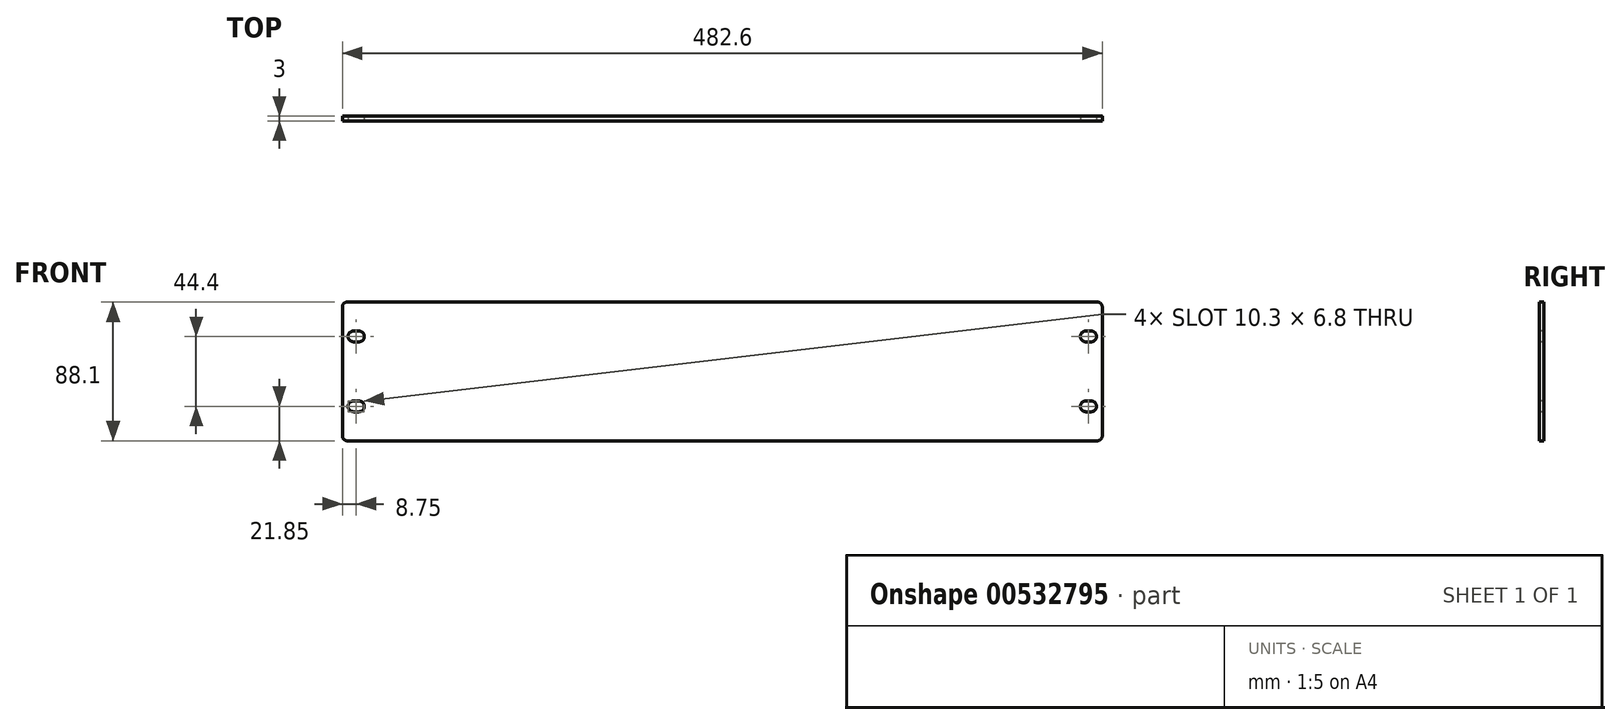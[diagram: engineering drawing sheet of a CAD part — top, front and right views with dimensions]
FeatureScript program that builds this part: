
annotation { "Feature Type Name" : "Feature", "Feature Type Description" : "" }
export const myFeature = defineFeature(function(context is Context, id is Id, definition is map)
    precondition{}
    {
        {
            var Q0;
            Q0=qCreatedBy(makeId("Front.planeOp"),FACE);
            var sketch = newSketch(context, id + "F0", { "sketchPlane" : qUnion([Q0])});
            skLineSegment(sketch, "E0.bottom", {"start": v(241.3, -44.05) * mm, "end": v(-241.3, -44.05) * mm});
            skLineSegment(sketch, "E0.top", {"start": v(241.3, 44.05) * mm, "end": v(-241.3, 44.05) * mm});
            skLineSegment(sketch, "E0.left", {"start": v(241.3, -44.05) * mm, "end": v(241.3, 44.05) * mm});
            skLineSegment(sketch, "E0.right", {"start": v(-241.3, -44.05) * mm, "end": v(-241.3, 44.05) * mm});
            skPoint(sketch, "E0.middle", {"position": v(0, 0) * mm});
            skSolve(sketch);
        }
        {
            var Q0;
            Q0=makeQuery(id+"F0.imprint","IMPRINT",FACE,{"disambiguationData":[TD([[makeQuery(id+"F0.imprint","IMPRINT",EDGE,{"derivedFrom":sQuery(id+"F0.wireOp",EDGE,"E0.bottom")}),-1.0]])]});
            extrude(context, id + "F1", {"entities" : qUnion([Q0]), "oppositeDirection" : true, "depth" : 3 * mm, "offsetDistance" : 25 * mm});
        }
        {
            var Q0;
            Q0=makeQuery(id+"F1.opExtrude","SWEPT_EDGE",EDGE,{"disambiguationData":[OSD([sQuery(id+"F0.wireOp",EDGE,"E0.top"),sQuery(id+"F0.wireOp",EDGE,"E0.right")])]});
            var Q1;
            Q1=makeQuery(id+"F1.opExtrude","SWEPT_EDGE",EDGE,{"disambiguationData":[OSD([sQuery(id+"F0.wireOp",EDGE,"E0.top"),sQuery(id+"F0.wireOp",EDGE,"E0.left")])]});
            var Q2;
            Q2=makeQuery(id+"F1.opExtrude","SWEPT_EDGE",EDGE,{"disambiguationData":[OSD([sQuery(id+"F0.wireOp",EDGE,"E0.bottom"),sQuery(id+"F0.wireOp",EDGE,"E0.left")])]});
            var Q3;
            Q3=makeQuery(id+"F1.opExtrude","SWEPT_EDGE",EDGE,{"disambiguationData":[OSD([sQuery(id+"F0.wireOp",EDGE,"E0.bottom"),sQuery(id+"F0.wireOp",EDGE,"E0.right")])]});
            fillet(context, id + "F2", {"entities" : qUnion([Q0, Q1, Q2, Q3]), "radius" : 3 * mm, "tangentPropagation" : true, "allowEdgeOverflow" : false});
        }
        {
            var Q0;
            Q0=qCreatedBy(makeId("Front.planeOp"),FACE);
            var sketch = newSketch(context, id + "F3", { "sketchPlane" : qUnion([Q0])});
            skArc(sketch, "E1", {"start": v(-230.8, 18.8) * mm, "mid": v(-227.4, 22.2) * mm, "end": v(-230.8, 25.6) * mm});
            skArc(sketch, "E2", {"start": v(-234.3, 25.6) * mm, "mid": v(-237.7, 22.2) * mm, "end": v(-234.3, 18.8) * mm});
            skLineSegment(sketch, "E3", {"start": v(-234.3, 25.6) * mm, "end": v(-230.8, 25.6) * mm});
            skLineSegment(sketch, "E4", {"start": v(-234.3, 18.8) * mm, "end": v(-230.8, 18.8) * mm});
            skArc(sketch, "E5.MirrorCS", {"start": v(230.8, 18.8) * mm, "mid": v(227.4, 22.2) * mm, "end": v(230.8, 25.6) * mm});
            skLineSegment(sketch, "E6.MirrorCS", {"start": v(234.3, 25.6) * mm, "end": v(230.8, 25.6) * mm});
            skArc(sketch, "E7.MirrorCS", {"start": v(234.3, 25.6) * mm, "mid": v(237.7, 22.2) * mm, "end": v(234.3, 18.8) * mm});
            skLineSegment(sketch, "E8.MirrorCS", {"start": v(234.3, 18.8) * mm, "end": v(230.8, 18.8) * mm});
            skArc(sketch, "E9.MirrorCS", {"start": v(234.3, -25.6) * mm, "mid": v(237.7, -22.2) * mm, "end": v(234.3, -18.8) * mm});
            skArc(sketch, "E10.MirrorCS", {"start": v(230.8, -18.8) * mm, "mid": v(227.4, -22.2) * mm, "end": v(230.8, -25.6) * mm});
            skLineSegment(sketch, "E11.MirrorCS", {"start": v(234.3, -18.8) * mm, "end": v(230.8, -18.8) * mm});
            skLineSegment(sketch, "E12.MirrorCS", {"start": v(234.3, -25.6) * mm, "end": v(230.8, -25.6) * mm});
            skArc(sketch, "E13.MirrorCS", {"start": v(-230.8, -18.8) * mm, "mid": v(-227.4, -22.2) * mm, "end": v(-230.8, -25.6) * mm});
            skLineSegment(sketch, "E14.MirrorCS", {"start": v(-234.3, -25.6) * mm, "end": v(-230.8, -25.6) * mm});
            skArc(sketch, "E15.MirrorCS", {"start": v(-234.3, -25.6) * mm, "mid": v(-237.7, -22.2) * mm, "end": v(-234.3, -18.8) * mm});
            skLineSegment(sketch, "E16.MirrorCS", {"start": v(-234.3, -18.8) * mm, "end": v(-230.8, -18.8) * mm});
            skSolve(sketch);
        }
        {
            var Q0;
            Q0 = qSketchRegion(id + "F3", true);
            extrude(context, id + "F4", {"entities" : qUnion([Q0]), "operationType" : NewBodyOperationType.REMOVE, "endBound" : BoundingType.UP_TO_NEXT, "oppositeDirection" : true, "depth" : 25 * mm, "offsetDistance" : 25 * mm});
        }
    });
